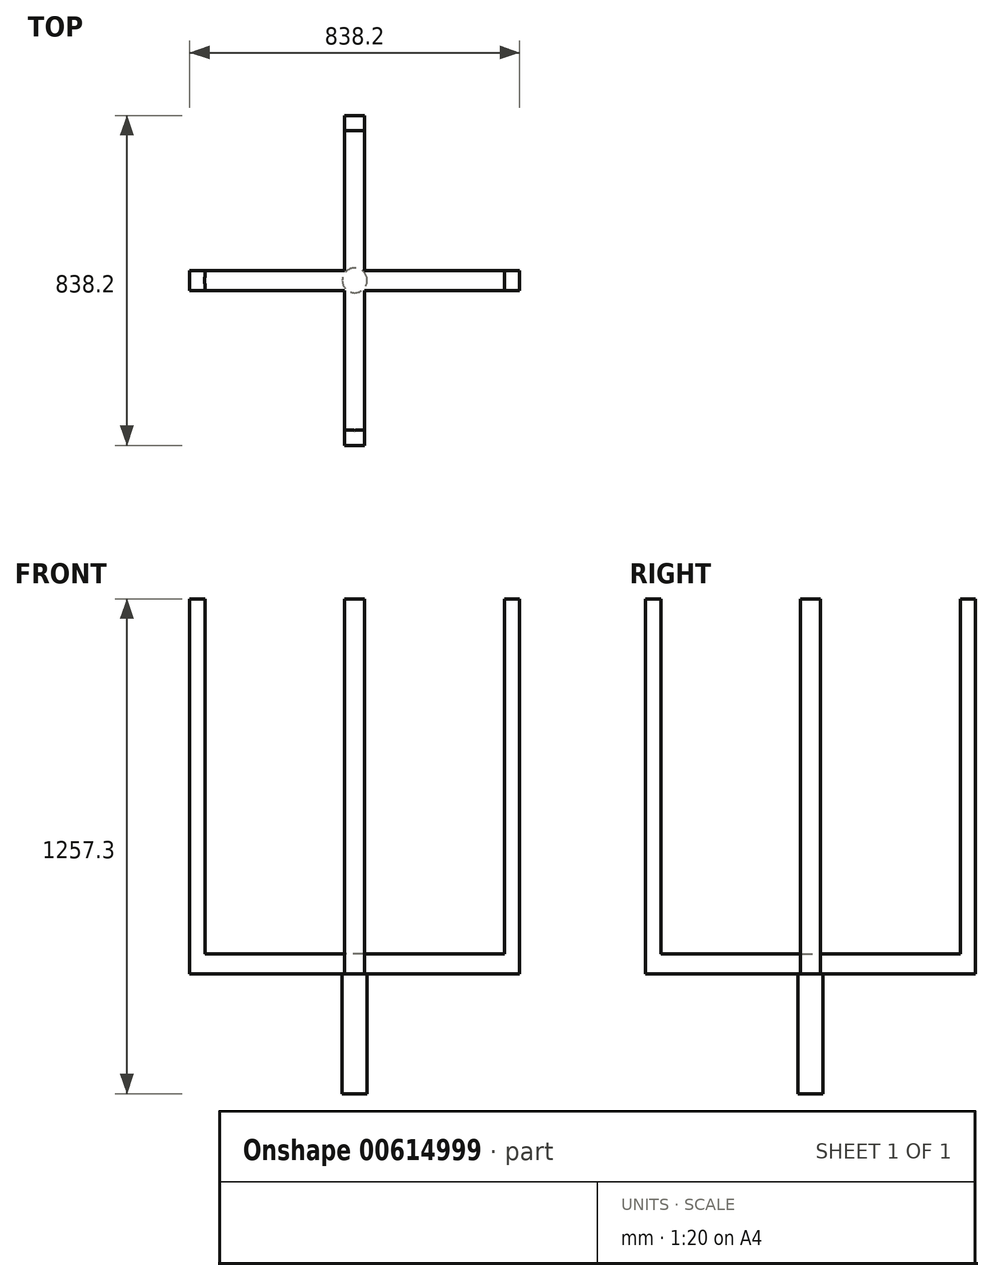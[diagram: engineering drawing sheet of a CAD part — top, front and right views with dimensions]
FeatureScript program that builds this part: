
annotation { "Feature Type Name" : "Feature", "Feature Type Description" : "" }
export const myFeature = defineFeature(function(context is Context, id is Id, definition is map)
    precondition{}
    {
        {
            var Q0;
            Q0=qCreatedBy(makeId("Top.planeOp"),FACE);
            var sketch = newSketch(context, id + "F0", { "sketchPlane" : qUnion([Q0])});
            skLineSegment(sketch, "E0.bottom", {"start": v(-25.4, 419.1) * mm, "end": v(25.4, 419.1) * mm});
            skLineSegment(sketch, "E0.top", {"start": v(-25.4, -419.1) * mm, "end": v(25.4, -419.1) * mm});
            skLineSegment(sketch, "E0.left", {"start": v(-25.4, 419.1) * mm, "end": v(-25.4, 25.4) * mm});
            skLineSegment(sketch, "E0.right", {"start": v(25.4, 419.1) * mm, "end": v(25.4, 25.4) * mm});
            skPoint(sketch, "E0.middle", {"position": v(0, 0) * mm});
            skLineSegment(sketch, "E1.bottom", {"start": v(419.1, 25.4) * mm, "end": v(25.4, 25.4) * mm});
            skLineSegment(sketch, "E1.top", {"start": v(419.1, -25.4) * mm, "end": v(25.4, -25.4) * mm});
            skLineSegment(sketch, "E1.left", {"start": v(419.1, 25.4) * mm, "end": v(419.1, -25.4) * mm});
            skLineSegment(sketch, "E1.right", {"start": v(-419.1, 25.4) * mm, "end": v(-419.1, -25.4) * mm});
            skLineSegment(sketch, "E2.trimOffspring", {"start": v(25.4, -25.4) * mm, "end": v(25.4, -419.1) * mm});
            skLineSegment(sketch, "E3.trimOffspring", {"start": v(-25.4, 25.4) * mm, "end": v(-419.1, 25.4) * mm});
            skLineSegment(sketch, "E4.trimOffspring", {"start": v(-25.4, -25.4) * mm, "end": v(-25.4, -419.1) * mm});
            skLineSegment(sketch, "E5.trimOffspring", {"start": v(-25.4, -25.4) * mm, "end": v(-419.1, -25.4) * mm});
            skSolve(sketch);
        }
        {
            var Q0;
            Q0=makeQuery(id+"F0.imprint","IMPRINT",FACE,{"disambiguationData":[TD([[makeQuery(id+"F0.imprint","IMPRINT",EDGE,{"derivedFrom":sQuery(id+"F0.wireOp",EDGE,"E0.bottom")}),-1.0]])]});
            extrude(context, id + "F1", {"entities" : qUnion([Q0]), "depth" : 50.8 * mm, "offsetDistance" : 25.4 * mm});
        }
        {
            var Q0;
            Q0=makeQuery(id+"F1.opExtrude","CAP_FACE",FACE,{"disambiguationData":[OSD([sQuery(id+"F0.wireOp",EDGE,"E0.bottom"),sQuery(id+"F0.wireOp",EDGE,"E0.top"),sQuery(id+"F0.wireOp",EDGE,"E0.left"),sQuery(id+"F0.wireOp",EDGE,"E0.right"),sQuery(id+"F0.wireOp",EDGE,"E1.bottom"),sQuery(id+"F0.wireOp",EDGE,"E1.top"),sQuery(id+"F0.wireOp",EDGE,"E1.left"),sQuery(id+"F0.wireOp",EDGE,"E1.right"),sQuery(id+"F0.wireOp",EDGE,"E2.trimOffspring"),sQuery(id+"F0.wireOp",EDGE,"E3.trimOffspring"),sQuery(id+"F0.wireOp",EDGE,"E4.trimOffspring"),sQuery(id+"F0.wireOp",EDGE,"E5.trimOffspring")])],"isStart":false});
            var sketch = newSketch(context, id + "F2", { "sketchPlane" : qUnion([Q0])});
            skCircle(sketch, "E6", {"center": v(0, 0) * mm, "radius": 381 * mm});
            skSolve(sketch);
        }
        {
            var Q0;
            {var subQ5=makeQuery(id+"F1.opExtrude","CAP_EDGE",EDGE,{"disambiguationData":[OSD([sQuery(id+"F0.wireOp",EDGE,"E0.bottom")])],"isStart":false});Q0=makeQuery(id+"F2.imprint","IMPRINT",FACE,{"disambiguationData":[TD([[makeQuery(id+"F2.imprint","IMPRINT",EDGE,{"derivedFrom":subQ5}),-1.0]])]});}
            var Q1;
            {var subQ5=makeQuery(id+"F1.opExtrude","CAP_EDGE",EDGE,{"disambiguationData":[OSD([sQuery(id+"F0.wireOp",EDGE,"E1.right")])],"isStart":false});Q1=makeQuery(id+"F2.imprint","IMPRINT",FACE,{"disambiguationData":[TD([[makeQuery(id+"F2.imprint","IMPRINT",EDGE,{"derivedFrom":subQ5}),1.0]])]});}
            var Q2;
            {var subQ5=makeQuery(id+"F1.opExtrude","CAP_EDGE",EDGE,{"disambiguationData":[OSD([sQuery(id+"F0.wireOp",EDGE,"E0.top")])],"isStart":false});Q2=makeQuery(id+"F2.imprint","IMPRINT",FACE,{"disambiguationData":[TD([[makeQuery(id+"F2.imprint","IMPRINT",EDGE,{"derivedFrom":subQ5}),1.0]])]});}
            var Q3;
            {var subQ5=makeQuery(id+"F1.opExtrude","CAP_EDGE",EDGE,{"disambiguationData":[OSD([sQuery(id+"F0.wireOp",EDGE,"E1.left")])],"isStart":false});Q3=makeQuery(id+"F2.imprint","IMPRINT",FACE,{"disambiguationData":[TD([[makeQuery(id+"F2.imprint","IMPRINT",EDGE,{"derivedFrom":subQ5}),-1.0]])]});}
            extrude(context, id + "F3", {"entities" : qUnion([Q0, Q1, Q2, Q3]), "operationType" : NewBodyOperationType.ADD, "depth" : 901.7 * mm, "offsetDistance" : 25.4 * mm});
        }
        {
            var Q0;
            Q0=makeQuery(id+"F1.opExtrude","CAP_FACE",FACE,{"disambiguationData":[OSD([sQuery(id+"F0.wireOp",EDGE,"E0.bottom"),sQuery(id+"F0.wireOp",EDGE,"E0.top"),sQuery(id+"F0.wireOp",EDGE,"E0.left"),sQuery(id+"F0.wireOp",EDGE,"E0.right"),sQuery(id+"F0.wireOp",EDGE,"E1.bottom"),sQuery(id+"F0.wireOp",EDGE,"E1.top"),sQuery(id+"F0.wireOp",EDGE,"E1.left"),sQuery(id+"F0.wireOp",EDGE,"E1.right"),sQuery(id+"F0.wireOp",EDGE,"E2.trimOffspring"),sQuery(id+"F0.wireOp",EDGE,"E3.trimOffspring"),sQuery(id+"F0.wireOp",EDGE,"E4.trimOffspring"),sQuery(id+"F0.wireOp",EDGE,"E5.trimOffspring")])],"isStart":true});
            var sketch = newSketch(context, id + "F4", { "sketchPlane" : qUnion([Q0])});
            skCircle(sketch, "E7", {"center": v(0, 0) * mm, "radius": 31.75 * mm});
            skSolve(sketch);
        }
        {
            var Q0;
            Q0 = qSketchRegion(id + "F4", true);
            extrude(context, id + "F5", {"entities" : qUnion([Q0]), "operationType" : NewBodyOperationType.ADD, "depth" : 304.8 * mm, "offsetDistance" : 25.4 * mm});
        }
    });
